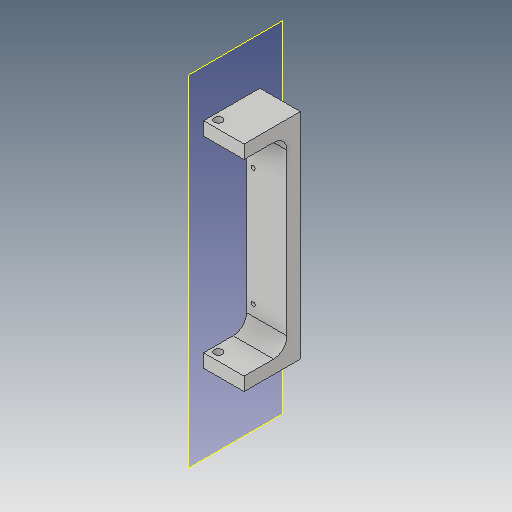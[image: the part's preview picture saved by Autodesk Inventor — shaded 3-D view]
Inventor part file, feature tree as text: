
AUTODESK INVENTOR PART (.ipt)
format: ipt  version: 2019.4 (Build 234330000, 330)  size: 129,024 bytes
history: native  units: mm
features: other x11, reference x6, sketch x3, plane x2, extrude x2, hole x1, projected_geometry x1
ambient origin geometry x8: Origin, YZ Plane, XZ Plane, XY Plane, X Axis, Y Axis, Z Axis, Center Point
bodies: Solid1 (feature_tree)
feature tree (26):
  plane  "Work Plane1"
  sketch  "Sketch1"  dims[d0=10.0mm d1=10.0mm]
  plane  "Work Plane2"
  extrude  "Extrusion1"  Depth=10.0mm
  extrude  "Extrusion2"  Depth=10.0mm
  hole  "Hole1"  [1 undecoded]
  reference  "Reference1"
  reference  "Reference2"
  reference  "Reference3"
  sketch  "Sketch2"  dims[d2=42.0mm d3=10.0mm]
  projected_geometry  "Projected Loop1"
  sketch  "Sketch3"  dims[d4=140.0mm d5=10.0mm d6=10.0mm d7=0.0mm d8=6.0mm d9=10.0mm d10=0.0mm d11=2.9mm d12=6.0mm d13=4.0mm d14=2.0mm d15=90.0deg d16=8.0mm d17=20.594885mm d18=0.0mm d19=6.0mm]
  reference  "Reference4"
  reference  "Reference5"
  reference  "Reference6"
  other  "Assembly_Opentrons_Imagingunit_v2.iam"
  other  "Assembly_opentrons_microscope_slide_y_base:1"
  other  "02_Opentrons_Microscope_Base_v0:1"
  other  "Assembly_Opentrons_Imagingunit_v1.iam"
  other  "Assembly_opentrons_microscope_slide_y:1"
  other  "Assembly_spindeldrive_350mm:1"
  other  "00_spindel_350mm:1"
  other  "Assembly_Opentrons_Autofocus_v1:1"
  other  "01_Slide_camera_x_rail:1"
  other  "04_OPENTRONS_Microscope_wellplate_base:1"
  other  "09_Opentrons_Microscope_Baseplate:1"
note: 1 required parameter value undecoded (feature->parameter linkage not recoverable at this tier; creation-order binding heuristic only, values carry confidence <= 0.55)
